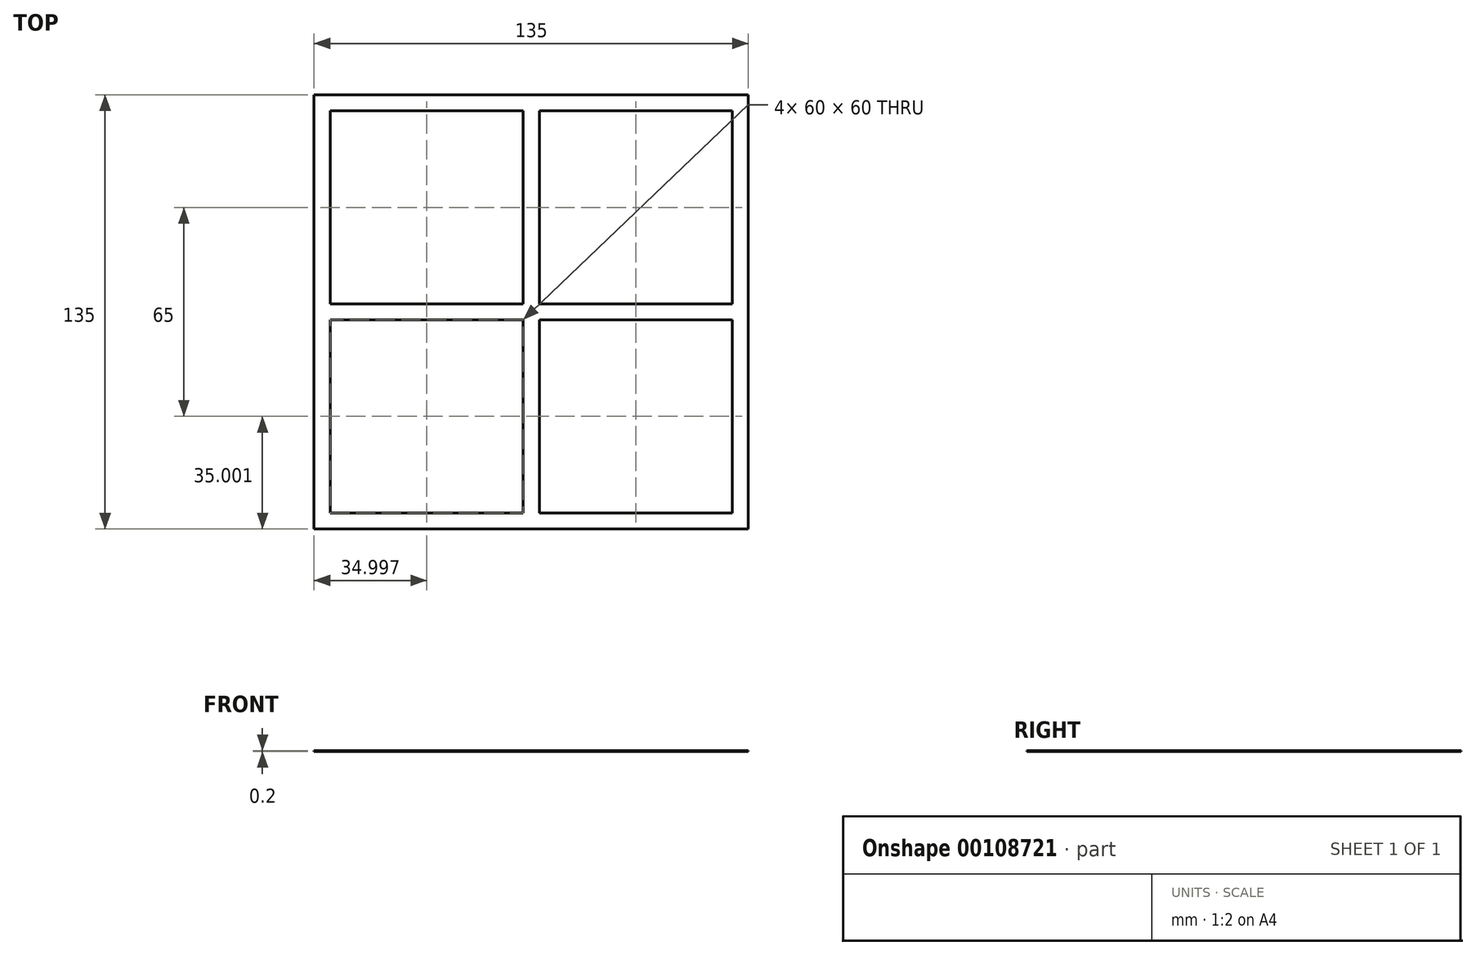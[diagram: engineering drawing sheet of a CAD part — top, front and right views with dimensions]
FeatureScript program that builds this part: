
annotation { "Feature Type Name" : "Feature", "Feature Type Description" : "" }
export const myFeature = defineFeature(function(context is Context, id is Id, definition is map)
    precondition{}
    {
        {
            var Q0;
            Q0=qCreatedBy(makeId("Top.planeOp"),FACE);
            var sketch = newSketch(context, id + "F0", { "sketchPlane" : qUnion([Q0])});
            skLineSegment(sketch, "E0.bottom", {"start": v(-68.48, 77.85) * mm, "end": v(66.52, 77.85) * mm});
            skLineSegment(sketch, "E0.top", {"start": v(-68.48, -57.15) * mm, "end": v(66.52, -57.15) * mm});
            skLineSegment(sketch, "E0.left", {"start": v(-68.48, 77.85) * mm, "end": v(-68.48, -57.15) * mm});
            skLineSegment(sketch, "E0.right", {"start": v(66.52, 77.85) * mm, "end": v(66.52, -57.15) * mm});
            skLineSegment(sketch, "E1", {"start": v(-68.48, 12.85) * mm, "end": v(66.52, 12.85) * mm});
            skLineSegment(sketch, "E2", {"start": v(-68.48, 7.85) * mm, "end": v(66.52, 7.85) * mm});
            skLineSegment(sketch, "E3", {"start": v(-3.48, 77.85) * mm, "end": v(-3.48, -57.15) * mm});
            skLineSegment(sketch, "E4", {"start": v(1.52, 77.85) * mm, "end": v(1.52, -57.15) * mm});
            skLineSegment(sketch, "E5", {"start": v(-68.48, -52.15) * mm, "end": v(66.52, -52.15) * mm});
            skLineSegment(sketch, "E6", {"start": v(-63.48, 77.85) * mm, "end": v(-63.48, -57.15) * mm});
            skLineSegment(sketch, "E7", {"start": v(-68.48, 72.85) * mm, "end": v(66.52, 72.85) * mm});
            skLineSegment(sketch, "E8", {"start": v(61.52, 77.85) * mm, "end": v(61.52, -57.15) * mm});
            skSolve(sketch);
        }
        {
            var Q0;
            {var subQ0=sQuery(id+"F0.wireOp",EDGE,"E1");var subQ1=sQuery(id+"F0.wireOp",EDGE,"E0.left");var subQ2=makeQuery(id+"F0.imprint","INTERSECT",VERTEX,{"derivedFrom":[subQ1,subQ0]});Q0=makeQuery(id+"F0.imprint","IMPRINT",FACE,{"disambiguationData":[TD([[makeQuery(id+"F0.imprint","IMPRINT",EDGE,{"disambiguationData":[TD([[subQ2,1.0]])],"derivedFrom":subQ1}),1.0]])]});}
            var Q1;
            {var subQ0=sQuery(id+"F0.wireOp",EDGE,"E0.left");var subQ1=sQuery(id+"F0.wireOp",EDGE,"E0.bottom");var subQ2=makeQuery(id+"F0.imprint","INTERSECT",VERTEX,{"derivedFrom":[subQ1,subQ0]});Q1=makeQuery(id+"F0.imprint","IMPRINT",FACE,{"disambiguationData":[TD([[makeQuery(id+"F0.imprint","IMPRINT",EDGE,{"disambiguationData":[TD([[subQ2,-1.0]])],"derivedFrom":subQ1}),-1.0]])]});}
            var Q2;
            {var subQ0=sQuery(id+"F0.wireOp",EDGE,"E3");var subQ1=sQuery(id+"F0.wireOp",EDGE,"E0.bottom");var subQ2=makeQuery(id+"F0.imprint","INTERSECT",VERTEX,{"derivedFrom":[subQ1,subQ0]});Q2=makeQuery(id+"F0.imprint","IMPRINT",FACE,{"disambiguationData":[TD([[makeQuery(id+"F0.imprint","IMPRINT",EDGE,{"disambiguationData":[TD([[subQ2,1.0]])],"derivedFrom":subQ1}),-1.0]])]});}
            var Q3;
            {var subQ0=sQuery(id+"F0.wireOp",EDGE,"E3");var subQ1=sQuery(id+"F0.wireOp",EDGE,"E0.bottom");var subQ2=makeQuery(id+"F0.imprint","INTERSECT",VERTEX,{"derivedFrom":[subQ1,subQ0]});Q3=makeQuery(id+"F0.imprint","IMPRINT",FACE,{"disambiguationData":[TD([[makeQuery(id+"F0.imprint","IMPRINT",EDGE,{"disambiguationData":[TD([[subQ2,-1.0]])],"derivedFrom":subQ1}),-1.0]])]});}
            var Q4;
            {var subQ0=sQuery(id+"F0.wireOp",EDGE,"E3");var subQ1=sQuery(id+"F0.wireOp",EDGE,"E1");var subQ2=makeQuery(id+"F0.imprint","INTERSECT",VERTEX,{"derivedFrom":[subQ1,subQ0]});Q4=makeQuery(id+"F0.imprint","IMPRINT",FACE,{"disambiguationData":[TD([[makeQuery(id+"F0.imprint","IMPRINT",EDGE,{"disambiguationData":[TD([[subQ2,-1.0]])],"derivedFrom":subQ1}),1.0]])]});}
            var Q5;
            {var subQ0=sQuery(id+"F0.wireOp",EDGE,"E4");var subQ1=sQuery(id+"F0.wireOp",EDGE,"E0.bottom");var subQ2=makeQuery(id+"F0.imprint","INTERSECT",VERTEX,{"derivedFrom":[subQ1,subQ0]});Q5=makeQuery(id+"F0.imprint","IMPRINT",FACE,{"disambiguationData":[TD([[makeQuery(id+"F0.imprint","IMPRINT",EDGE,{"disambiguationData":[TD([[subQ2,-1.0]])],"derivedFrom":subQ1}),-1.0]])]});}
            var Q6;
            {var subQ0=sQuery(id+"F0.wireOp",EDGE,"E0.right");var subQ1=sQuery(id+"F0.wireOp",EDGE,"E0.bottom");var subQ2=makeQuery(id+"F0.imprint","INTERSECT",VERTEX,{"derivedFrom":[subQ1,subQ0]});Q6=makeQuery(id+"F0.imprint","IMPRINT",FACE,{"disambiguationData":[TD([[makeQuery(id+"F0.imprint","IMPRINT",EDGE,{"disambiguationData":[TD([[subQ2,1.0]])],"derivedFrom":subQ1}),-1.0]])]});}
            var Q7;
            {var subQ0=sQuery(id+"F0.wireOp",EDGE,"E1");var subQ1=sQuery(id+"F0.wireOp",EDGE,"E0.right");var subQ2=makeQuery(id+"F0.imprint","INTERSECT",VERTEX,{"derivedFrom":[subQ1,subQ0]});Q7=makeQuery(id+"F0.imprint","IMPRINT",FACE,{"disambiguationData":[TD([[makeQuery(id+"F0.imprint","IMPRINT",EDGE,{"disambiguationData":[TD([[subQ2,1.0]])],"derivedFrom":subQ1}),-1.0]])]});}
            var Q8;
            {var subQ0=sQuery(id+"F0.wireOp",EDGE,"E1");var subQ1=sQuery(id+"F0.wireOp",EDGE,"E0.right");var subQ2=makeQuery(id+"F0.imprint","INTERSECT",VERTEX,{"derivedFrom":[subQ1,subQ0]});Q8=makeQuery(id+"F0.imprint","IMPRINT",FACE,{"disambiguationData":[TD([[makeQuery(id+"F0.imprint","IMPRINT",EDGE,{"disambiguationData":[TD([[subQ2,-1.0]])],"derivedFrom":subQ1}),-1.0]])]});}
            var Q9;
            {var subQ0=sQuery(id+"F0.wireOp",EDGE,"E4");var subQ1=sQuery(id+"F0.wireOp",EDGE,"E1");var subQ2=makeQuery(id+"F0.imprint","INTERSECT",VERTEX,{"derivedFrom":[subQ1,subQ0]});Q9=makeQuery(id+"F0.imprint","IMPRINT",FACE,{"disambiguationData":[TD([[makeQuery(id+"F0.imprint","IMPRINT",EDGE,{"disambiguationData":[TD([[subQ2,-1.0]])],"derivedFrom":subQ1}),-1.0]])]});}
            var Q10;
            {var subQ0=sQuery(id+"F0.wireOp",EDGE,"E3");var subQ1=sQuery(id+"F0.wireOp",EDGE,"E1");var subQ2=makeQuery(id+"F0.imprint","INTERSECT",VERTEX,{"derivedFrom":[subQ1,subQ0]});Q10=makeQuery(id+"F0.imprint","IMPRINT",FACE,{"disambiguationData":[TD([[makeQuery(id+"F0.imprint","IMPRINT",EDGE,{"disambiguationData":[TD([[subQ2,-1.0]])],"derivedFrom":subQ1}),-1.0]])]});}
            var Q11;
            {var subQ0=sQuery(id+"F0.wireOp",EDGE,"E6");var subQ1=sQuery(id+"F0.wireOp",EDGE,"E1");var subQ2=makeQuery(id+"F0.imprint","INTERSECT",VERTEX,{"derivedFrom":[subQ1,subQ0]});Q11=makeQuery(id+"F0.imprint","IMPRINT",FACE,{"disambiguationData":[TD([[makeQuery(id+"F0.imprint","IMPRINT",EDGE,{"disambiguationData":[TD([[subQ2,-1.0]])],"derivedFrom":subQ1}),-1.0]])]});}
            var Q12;
            {var subQ0=sQuery(id+"F0.wireOp",EDGE,"E1");var subQ1=sQuery(id+"F0.wireOp",EDGE,"E0.left");var subQ2=makeQuery(id+"F0.imprint","INTERSECT",VERTEX,{"derivedFrom":[subQ1,subQ0]});Q12=makeQuery(id+"F0.imprint","IMPRINT",FACE,{"disambiguationData":[TD([[makeQuery(id+"F0.imprint","IMPRINT",EDGE,{"disambiguationData":[TD([[subQ2,-1.0]])],"derivedFrom":subQ1}),1.0]])]});}
            var Q13;
            {var subQ0=sQuery(id+"F0.wireOp",EDGE,"E2");var subQ1=sQuery(id+"F0.wireOp",EDGE,"E0.left");var subQ2=makeQuery(id+"F0.imprint","INTERSECT",VERTEX,{"derivedFrom":[subQ1,subQ0]});Q13=makeQuery(id+"F0.imprint","IMPRINT",FACE,{"disambiguationData":[TD([[makeQuery(id+"F0.imprint","IMPRINT",EDGE,{"disambiguationData":[TD([[subQ2,-1.0]])],"derivedFrom":subQ1}),1.0]])]});}
            var Q14;
            {var subQ0=sQuery(id+"F0.wireOp",EDGE,"E3");var subQ1=sQuery(id+"F0.wireOp",EDGE,"E2");var subQ2=makeQuery(id+"F0.imprint","INTERSECT",VERTEX,{"derivedFrom":[subQ1,subQ0]});Q14=makeQuery(id+"F0.imprint","IMPRINT",FACE,{"disambiguationData":[TD([[makeQuery(id+"F0.imprint","IMPRINT",EDGE,{"disambiguationData":[TD([[subQ2,-1.0]])],"derivedFrom":subQ1}),-1.0]])]});}
            var Q15;
            {var subQ0=sQuery(id+"F0.wireOp",EDGE,"E0.left");var subQ1=sQuery(id+"F0.wireOp",EDGE,"E0.top");var subQ2=makeQuery(id+"F0.imprint","INTERSECT",VERTEX,{"derivedFrom":[subQ1,subQ0]});Q15=makeQuery(id+"F0.imprint","IMPRINT",FACE,{"disambiguationData":[TD([[makeQuery(id+"F0.imprint","IMPRINT",EDGE,{"disambiguationData":[TD([[subQ2,-1.0]])],"derivedFrom":subQ1}),1.0]])]});}
            var Q16;
            {var subQ0=sQuery(id+"F0.wireOp",EDGE,"E3");var subQ1=sQuery(id+"F0.wireOp",EDGE,"E0.top");var subQ2=makeQuery(id+"F0.imprint","INTERSECT",VERTEX,{"derivedFrom":[subQ1,subQ0]});Q16=makeQuery(id+"F0.imprint","IMPRINT",FACE,{"disambiguationData":[TD([[makeQuery(id+"F0.imprint","IMPRINT",EDGE,{"disambiguationData":[TD([[subQ2,1.0]])],"derivedFrom":subQ1}),1.0]])]});}
            var Q17;
            {var subQ0=sQuery(id+"F0.wireOp",EDGE,"E3");var subQ1=sQuery(id+"F0.wireOp",EDGE,"E0.top");var subQ2=makeQuery(id+"F0.imprint","INTERSECT",VERTEX,{"derivedFrom":[subQ1,subQ0]});Q17=makeQuery(id+"F0.imprint","IMPRINT",FACE,{"disambiguationData":[TD([[makeQuery(id+"F0.imprint","IMPRINT",EDGE,{"disambiguationData":[TD([[subQ2,-1.0]])],"derivedFrom":subQ1}),1.0]])]});}
            var Q18;
            {var subQ0=sQuery(id+"F0.wireOp",EDGE,"E4");var subQ1=sQuery(id+"F0.wireOp",EDGE,"E0.top");var subQ2=makeQuery(id+"F0.imprint","INTERSECT",VERTEX,{"derivedFrom":[subQ1,subQ0]});Q18=makeQuery(id+"F0.imprint","IMPRINT",FACE,{"disambiguationData":[TD([[makeQuery(id+"F0.imprint","IMPRINT",EDGE,{"disambiguationData":[TD([[subQ2,-1.0]])],"derivedFrom":subQ1}),1.0]])]});}
            var Q19;
            {var subQ0=sQuery(id+"F0.wireOp",EDGE,"E0.right");var subQ1=sQuery(id+"F0.wireOp",EDGE,"E0.top");var subQ2=makeQuery(id+"F0.imprint","INTERSECT",VERTEX,{"derivedFrom":[subQ1,subQ0]});Q19=makeQuery(id+"F0.imprint","IMPRINT",FACE,{"disambiguationData":[TD([[makeQuery(id+"F0.imprint","IMPRINT",EDGE,{"disambiguationData":[TD([[subQ2,1.0]])],"derivedFrom":subQ1}),1.0]])]});}
            var Q20;
            {var subQ0=sQuery(id+"F0.wireOp",EDGE,"E2");var subQ1=sQuery(id+"F0.wireOp",EDGE,"E0.right");var subQ2=makeQuery(id+"F0.imprint","INTERSECT",VERTEX,{"derivedFrom":[subQ1,subQ0]});Q20=makeQuery(id+"F0.imprint","IMPRINT",FACE,{"disambiguationData":[TD([[makeQuery(id+"F0.imprint","IMPRINT",EDGE,{"disambiguationData":[TD([[subQ2,-1.0]])],"derivedFrom":subQ1}),-1.0]])]});}
            extrude(context, id + "F1", {"entities" : qUnion([Q0, Q1, Q2, Q3, Q4, Q5, Q6, Q7, Q8, Q9, Q10, Q11, Q12, Q13, Q14, Q15, Q16, Q17, Q18, Q19, Q20]), "depth" : 0.2 * mm});
        }
    });
